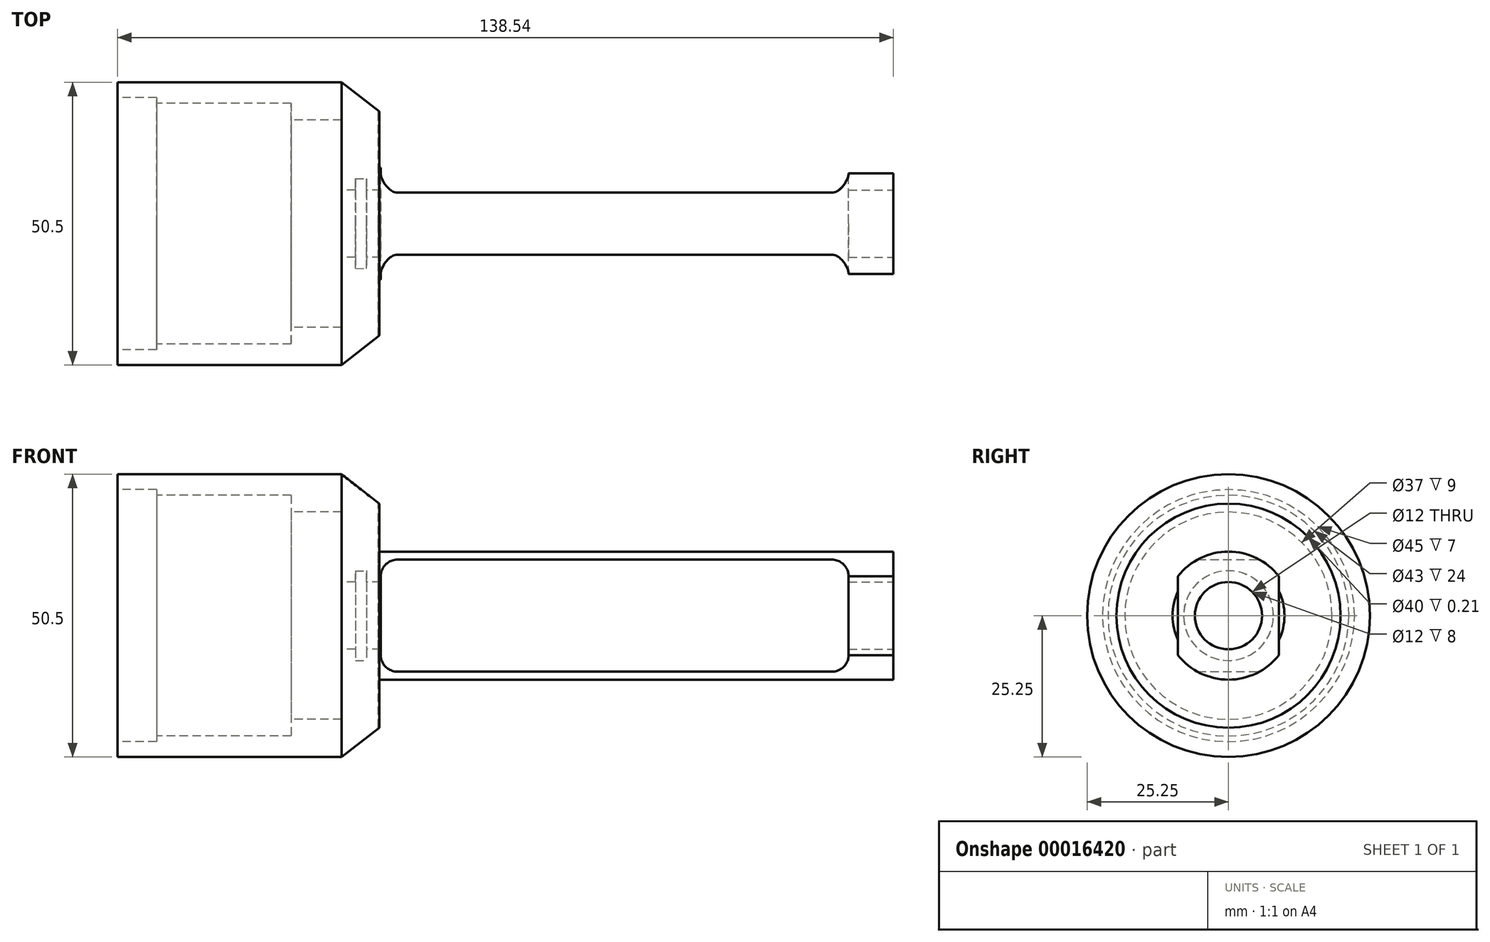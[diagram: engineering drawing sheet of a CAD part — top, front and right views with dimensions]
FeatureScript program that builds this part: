
annotation { "Feature Type Name" : "Feature", "Feature Type Description" : "" }
export const myFeature = defineFeature(function(context is Context, id is Id, definition is map)
    precondition{}
    {
        {
            var Q0;
            Q0=qCreatedBy(makeId("Front.planeOp"),FACE);
            var sketch = newSketch(context, id + "F0", { "sketchPlane" : qUnion([Q0])});
            skLineSegment(sketch, "E0", {"start": v(-43.3, 0) * mm, "end": v(90.49, 0) * mm, "construction": true});
            skLineSegment(sketch, "E1", {"start": v(6.7, 20) * mm, "end": v(90.49, 20) * mm});
            skLineSegment(sketch, "E2", {"start": v(90.49, 20) * mm, "end": v(98.49, 11.43) * mm});
            skLineSegment(sketch, "E3", {"start": v(98.49, 11.43) * mm, "end": v(98.49, 0) * mm});
            skLineSegment(sketch, "E4", {"start": v(98.49, 0) * mm, "end": v(90.49, 0) * mm});
            skLineSegment(sketch, "E5", {"start": v(90.49, 0) * mm, "end": v(90.49, 10) * mm});
            skLineSegment(sketch, "E6", {"start": v(90.49, 10) * mm, "end": v(6.95, 10) * mm});
            skLineSegment(sketch, "E7", {"start": v(6.95, 10) * mm, "end": v(6.95, 6) * mm});
            skLineSegment(sketch, "E8", {"start": v(4.45, 6.02) * mm, "end": v(4.44, 8.02) * mm});
            skLineSegment(sketch, "E9", {"start": v(4.44, 8.02) * mm, "end": v(2.43, 8) * mm});
            skLineSegment(sketch, "E10", {"start": v(2.43, 8) * mm, "end": v(2.45, 6) * mm});
            skLineSegment(sketch, "E11", {"start": v(-0.05, 6) * mm, "end": v(-0.05, 18.5) * mm});
            skLineSegment(sketch, "E12", {"start": v(-40.05, 25.25) * mm, "end": v(-0.05, 25.25) * mm});
            skLineSegment(sketch, "E13.0", {"start": v(-40.05, 22.5) * mm, "end": v(-33.05, 22.5) * mm});
            skLineSegment(sketch, "E14.0", {"start": v(-33.05, 21.5) * mm, "end": v(-9.05, 21.5) * mm});
            skLineSegment(sketch, "E15.0", {"start": v(-33.05, 22.5) * mm, "end": v(-33.05, 21.5) * mm});
            skLineSegment(sketch, "E16.0", {"start": v(-9.05, 18.5) * mm, "end": v(-0.05, 18.5) * mm});
            skLineSegment(sketch, "E17.0", {"start": v(-9.05, 18.5) * mm, "end": v(-9.05, 21.5) * mm});
            skLineSegment(sketch, "E18", {"start": v(-0.05, 25.25) * mm, "end": v(6.7, 20) * mm});
            skLineSegment(sketch, "E19", {"start": v(-40.05, 22.5) * mm, "end": v(-40.05, 25.25) * mm});
            skLineSegment(sketch, "E20", {"start": v(-0.05, 6) * mm, "end": v(2.45, 6) * mm});
            skPoint(sketch, "E21.end.orphan", {"position": v(2.45, 5.6) * mm});
            skLineSegment(sketch, "E22.trimOffspring", {"start": v(4.45, 6.02) * mm, "end": v(6.95, 6) * mm});
            skSolve(sketch);
        }
        {
            var Q0;
            Q0=makeQuery(id+"F0.imprint","IMPRINT",FACE,{"disambiguationData":[TD([[makeQuery(id+"F0.imprint","IMPRINT",EDGE,{"derivedFrom":sQuery(id+"F0.wireOp",EDGE,"E1")}),-1.0]])]});
            var Q1;
            Q1=sQuery(id+"F0.wireOp",EDGE,"E0");
            revolve(context, id + "F1", {"entities" : qUnion([Q0]), "axis" : qUnion([Q1]), "revolveType" : RevolveType.FULL});
        }
        {
            var Q0;
            Q0=makeQuery(id+"F1.opRevolve","SWEPT_FACE",FACE,{"disambiguationData":[OSD([sQuery(id+"F0.wireOp",EDGE,"E3")])]});
            var sketch = newSketch(context, id + "F2", { "sketchPlane" : qUnion([Q0])});
            skLineSegment(sketch, "E23.0", {"start": v(9, -17.86) * mm, "end": v(9, 17.86) * mm});
            skLineSegment(sketch, "E24.0", {"start": v(-9, -17.86) * mm, "end": v(-9, 17.86) * mm});
            skCircle(sketch, "E25.0", {"center": v(0, 0) * mm, "radius": 20 * mm});
            skCircle(sketch, "E26.0", {"center": v(0, 0) * mm, "radius": 11.43 * mm});
            skCircle(sketch, "E27", {"center": v(0, 0) * mm, "radius": 6 * mm});
            skSolve(sketch);
        }
        {
            var Q0;
            {var subQ1=sQuery(id+"F2.wireOp",EDGE,"E24.0");var subQ4=sQuery(id+"F2.wireOp",EDGE,"E25.0");var subQ6=makeQuery(id+"F2.imprint","INTERSECT",VERTEX,{"disambiguationData":[OD(0.0)],"derivedFrom":[subQ1,subQ4]});Q0=makeQuery(id+"F2.imprint","IMPRINT",FACE,{"disambiguationData":[TD([[makeQuery(id+"F2.imprint","IMPRINT",EDGE,{"disambiguationData":[TD([[subQ6,1.0]])],"derivedFrom":subQ4}),1.0]])]});}
            var Q1;
            {var subQ0=makeQuery(id+"F1.opRevolve","SWEPT_EDGE",EDGE,{"disambiguationData":[OSD([sQuery(id+"F0.wireOp",EDGE,"E2"),sQuery(id+"F0.wireOp",EDGE,"E3")])]});var subQ1=sQuery(id+"F2.wireOp",EDGE,"E24.0");var subQ3=makeQuery(id+"F2.imprint","INTERSECT",VERTEX,{"disambiguationData":[OD(0.0)],"derivedFrom":[subQ0,subQ1]});Q1=makeQuery(id+"F2.imprint","IMPRINT",FACE,{"disambiguationData":[TD([[makeQuery(id+"F2.imprint","IMPRINT",EDGE,{"disambiguationData":[TD([[subQ3,-1.0]])],"derivedFrom":subQ1}),1.0]])]});}
            var Q2;
            {var subQ1=sQuery(id+"F2.wireOp",EDGE,"E23.0");var subQ4=sQuery(id+"F2.wireOp",EDGE,"E25.0");var subQ6=makeQuery(id+"F2.imprint","INTERSECT",VERTEX,{"disambiguationData":[OD(0.0)],"derivedFrom":[subQ1,subQ4]});Q2=makeQuery(id+"F2.imprint","IMPRINT",FACE,{"disambiguationData":[TD([[makeQuery(id+"F2.imprint","IMPRINT",EDGE,{"disambiguationData":[TD([[subQ6,-1.0]])],"derivedFrom":subQ4}),1.0]])]});}
            var Q3;
            {var subQ0=makeQuery(id+"F1.opRevolve","SWEPT_EDGE",EDGE,{"disambiguationData":[OSD([sQuery(id+"F0.wireOp",EDGE,"E2"),sQuery(id+"F0.wireOp",EDGE,"E3")])]});var subQ1=sQuery(id+"F2.wireOp",EDGE,"E23.0");var subQ3=makeQuery(id+"F2.imprint","INTERSECT",VERTEX,{"disambiguationData":[OD(0.0)],"derivedFrom":[subQ0,subQ1]});Q3=makeQuery(id+"F2.imprint","IMPRINT",FACE,{"disambiguationData":[TD([[makeQuery(id+"F2.imprint","IMPRINT",EDGE,{"disambiguationData":[TD([[subQ3,-1.0]])],"derivedFrom":subQ1}),-1.0]])]});}
            extrude(context, id + "F3", {"entities" : qUnion([Q0, Q1, Q2, Q3]), "operationType" : NewBodyOperationType.REMOVE, "oppositeDirection" : true, "depth" : 62 * mm});
        }
        {
            var Q0;
            Q0=qCreatedBy(makeId("Right.planeOp"),FACE);
            cPlane(context, id + "F4", {"entities" : qUnion([Q0]), "cplaneType" : CPlaneType.OFFSET, "offset" : 40 * mm, "width" : 150 * mm, "height" : 150 * mm});
        }
        {
            var Q0;
            Q0=qCreatedBy(id+"F4.planeOp",FACE);
            var sketch = newSketch(context, id + "F5", { "sketchPlane" : qUnion([Q0])});
            skArc(sketch, "E28.0.0", {"start": v(9, 4.36) * mm, "mid": v(0, 10) * mm, "end": v(-9, 4.36) * mm});
            skLineSegment(sketch, "E28.0.1", {"start": v(-9, 4.36) * mm, "end": v(-9, 13.92) * mm});
            skArc(sketch, "E28.0.2", {"start": v(-9, 13.92) * mm, "mid": v(-16.58, -1.1) * mm, "end": v(-8, -15.56) * mm});
            skLineSegment(sketch, "E28.0.3", {"start": v(-8, -15.56) * mm, "end": v(-8, -6) * mm});
            skArc(sketch, "E28.0.4", {"start": v(-8, -6) * mm, "mid": v(0.96, -9.95) * mm, "end": v(9, -4.36) * mm});
            skLineSegment(sketch, "E28.0.5", {"start": v(9, -4.36) * mm, "end": v(9, -13.92) * mm});
            skArc(sketch, "E28.0.6", {"start": v(9, -13.92) * mm, "mid": v(15.9, 0) * mm, "end": v(9, 13.92) * mm});
            skLineSegment(sketch, "E28.0.7", {"start": v(9, 13.92) * mm, "end": v(9, 4.36) * mm});
            skCircle(sketch, "E29", {"center": v(0, 0) * mm, "radius": 6 * mm});
            skSolve(sketch);
        }
        {
            var Q0;
            Q0=makeQuery(id+"F5.imprint","IMPRINT",FACE,{"disambiguationData":[TD([[makeQuery(id+"F5.imprint","IMPRINT",EDGE,{"derivedFrom":sQuery(id+"F5.wireOp",EDGE,"E29")}),1.0]])]});
            extrude(context, id + "F6", {"entities" : qUnion([Q0]), "depth" : 50 * mm});
        }
        {
            var Q0;
            Q0=makeQuery(id+"F6.opExtrude","SWEPT_BODY",BODY,{"disambiguationData":[OSD([sQuery(id+"F5.wireOp",EDGE,"E29")])]});
            var Q1;
            Q1=makeQuery(id+"F1.opRevolve","SWEPT_BODY",BODY,{"disambiguationData":[OSD([sQuery(id+"F0.wireOp",EDGE,"E1"),sQuery(id+"F0.wireOp",EDGE,"E2"),sQuery(id+"F0.wireOp",EDGE,"E3"),sQuery(id+"F0.wireOp",EDGE,"E4"),sQuery(id+"F0.wireOp",EDGE,"E5"),sQuery(id+"F0.wireOp",EDGE,"E6"),sQuery(id+"F0.wireOp",EDGE,"E7"),sQuery(id+"F0.wireOp",EDGE,"cb62e50a-a9be-4bb2-b454-aeddb4c2251b"),sQuery(id+"F0.wireOp",EDGE,"E8"),sQuery(id+"F0.wireOp",EDGE,"E9"),sQuery(id+"F0.wireOp",EDGE,"E10"),sQuery(id+"F0.wireOp",EDGE,"E11"),sQuery(id+"F0.wireOp",EDGE,"E12"),sQuery(id+"F0.wireOp",EDGE,"E13.0"),sQuery(id+"F0.wireOp",EDGE,"E14.0"),sQuery(id+"F0.wireOp",EDGE,"E15.0"),sQuery(id+"F0.wireOp",EDGE,"de0d1e02-c222-4410-acb6-474e92f1eed9"),sQuery(id+"F0.wireOp",EDGE,"E21"),sQuery(id+"F0.wireOp",EDGE,"E16.0"),sQuery(id+"F0.wireOp",EDGE,"E17.0"),sQuery(id+"F0.wireOp",EDGE,"E18")])]});
            booleanBodies(context, id + "F7", {"operationType" : BooleanOperationType.SUBTRACTION, "tools" : qUnion([Q0]), "targets" : qUnion([Q1])});
        }
        {
            var Q0;
            Q0=makeQuery(id+"F3.boolean.opBoolean","COPY",FACE,{"derivedFrom":makeQuery(id+"F3.opExtrude","CAP_FACE",FACE,{"disambiguationData":[OSD([sQuery(id+"F2.wireOp",EDGE,"E24.0"),sQuery(id+"F2.wireOp",EDGE,"E25.0")])],"isStart":false})});
            var Q1;
            Q1=makeQuery(id+"F3.boolean.opBoolean","COPY",FACE,{"derivedFrom":makeQuery(id+"F3.opExtrude","CAP_FACE",FACE,{"disambiguationData":[OSD([sQuery(id+"F2.wireOp",EDGE,"E23.0"),sQuery(id+"F2.wireOp",EDGE,"E25.0")])],"isStart":false})});
            extrude(context, id + "F8", {"entities" : qUnion([Q0, Q1]), "operationType" : NewBodyOperationType.REMOVE, "oppositeDirection" : true, "depth" : 30 * mm});
        }
        {
            var Q0;
            Q0=makeQuery(id+"F1.opRevolve","SWEPT_FACE",FACE,{"disambiguationData":[OSD([sQuery(id+"F0.wireOp",EDGE,"E3")])]});
            var sketch = newSketch(context, id + "F9", { "sketchPlane" : qUnion([Q0])});
            skCircle(sketch, "E30", {"center": v(0, 0) * mm, "radius": 6 * mm});
            skSolve(sketch);
        }
        {
            var Q0;
            Q0=makeQuery(id+"F9.imprint","IMPRINT",FACE,{"disambiguationData":[TD([[makeQuery(id+"F9.imprint","IMPRINT",EDGE,{"derivedFrom":sQuery(id+"F9.wireOp",EDGE,"E30")}),1.0]])]});
            extrude(context, id + "F10", {"entities" : qUnion([Q0]), "operationType" : NewBodyOperationType.REMOVE, "oppositeDirection" : true, "depth" : 25 * mm});
        }
        {
            var Q0;
            Q0=qCreatedBy(makeId("Front.planeOp"),FACE);
            var sketch = newSketch(context, id + "F11", { "sketchPlane" : qUnion([Q0])});
            skLineSegment(sketch, "E31.0", {"start": v(90.49, 10) * mm, "end": v(6.95, 10) * mm});
            skLineSegment(sketch, "E32.0", {"start": v(90.49, 0) * mm, "end": v(90.49, 10) * mm});
            skLineSegment(sketch, "E33.0", {"start": v(6.95, 10) * mm, "end": v(6.95, 0) * mm});
            skLineSegment(sketch, "E34.0", {"start": v(-43.3, 0) * mm, "end": v(90.49, 0) * mm});
            skPoint(sketch, "E35.orphan", {"position": v(6.95, 6) * mm});
            skLineSegment(sketch, "E36.MirrorCS", {"start": v(90.49, 0) * mm, "end": v(90.49, -10) * mm});
            skLineSegment(sketch, "E37.MirrorCS", {"start": v(90.49, -10) * mm, "end": v(6.95, -10) * mm});
            skLineSegment(sketch, "E38.MirrorCS", {"start": v(6.95, -10) * mm, "end": v(6.95, 0) * mm});
            skLineSegment(sketch, "E39.left", {"start": v(90.49, 10) * mm, "end": v(90.49, -10) * mm});
            skLineSegment(sketch, "E39.right", {"start": v(6.95, 10) * mm, "end": v(6.95, -10) * mm});
            skSolve(sketch);
        }
        {
            var Q0;
            Q0 = qSketchRegion(id + "F11", true);
            extrude(context, id + "F12", {"entities" : qUnion([Q0]), "operationType" : NewBodyOperationType.REMOVE, "endBound" : BoundingType.SYMMETRIC, "depth" : 25 * mm});
        }
        {
            var Q0;
            Q0=makeQuery(id+"F12.boolean.opBoolean","COPY",EDGE,{"derivedFrom":makeQuery(id+"F12.opExtrude","SWEPT_EDGE",EDGE,{"disambiguationData":[OSD([sQuery(id+"F11.wireOp",EDGE,"E31.0"),sQuery(id+"F11.wireOp",EDGE,"E39.left")])]})});
            var Q1;
            Q1=makeQuery(id+"F12.boolean.opBoolean","COPY",EDGE,{"derivedFrom":makeQuery(id+"F12.opExtrude","SWEPT_EDGE",EDGE,{"disambiguationData":[OSD([sQuery(id+"F11.wireOp",EDGE,"E37.MirrorCS"),sQuery(id+"F11.wireOp",EDGE,"E39.left")])]})});
            fillet(context, id + "F13", {"entities" : qUnion([Q0, Q1]), "radius" : 3 * mm, "tangentPropagation" : true, "allowEdgeOverflow" : false});
        }
    });
